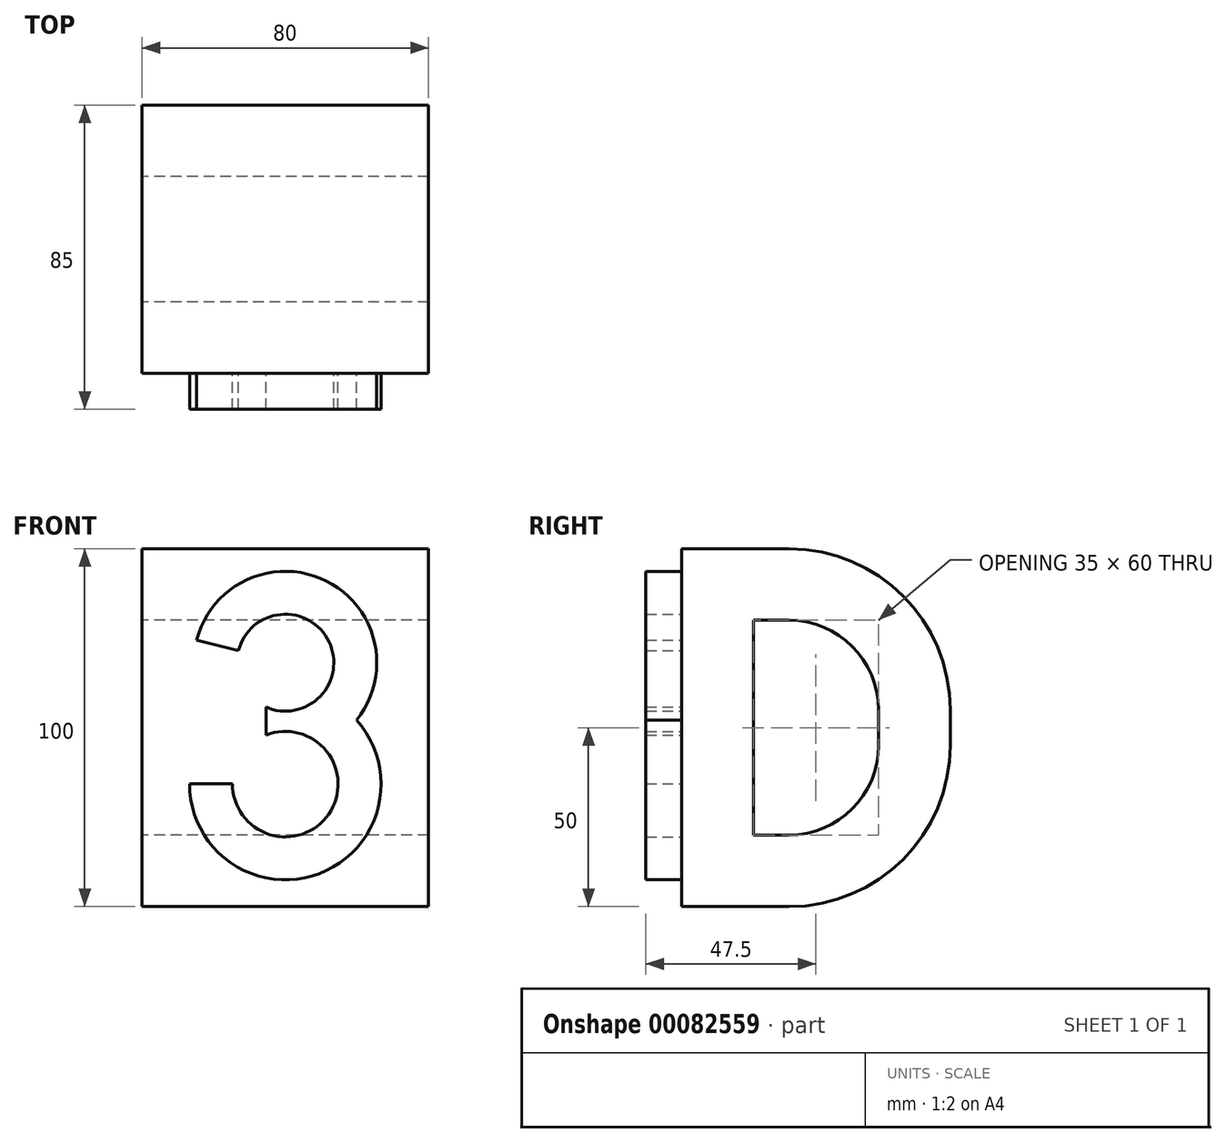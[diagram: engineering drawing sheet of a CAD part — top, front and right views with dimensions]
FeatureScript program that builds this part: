
annotation { "Feature Type Name" : "Feature", "Feature Type Description" : "" }
export const myFeature = defineFeature(function(context is Context, id is Id, definition is map)
    precondition{}
    {
        {
            var Q0;
            Q0=qCreatedBy(makeId("Right.planeOp"),FACE);
            var sketch = newSketch(context, id + "F0", { "sketchPlane" : qUnion([Q0])});
            skLineSegment(sketch, "E0.bottom", {"start": v(0, 0) * mm, "end": v(75, 0) * mm});
            skLineSegment(sketch, "E0.top", {"start": v(0, 100) * mm, "end": v(75, 100) * mm});
            skLineSegment(sketch, "E0.left", {"start": v(0, 0) * mm, "end": v(0, 100) * mm});
            skLineSegment(sketch, "E0.right", {"start": v(75, 0) * mm, "end": v(75, 100) * mm});
            skLineSegment(sketch, "E1.0", {"start": v(20, 80) * mm, "end": v(55, 80) * mm});
            skLineSegment(sketch, "E1.1", {"start": v(20, 20) * mm, "end": v(20, 80) * mm});
            skLineSegment(sketch, "E1.2", {"start": v(20, 20) * mm, "end": v(55, 20) * mm});
            skLineSegment(sketch, "E1.3", {"start": v(55, 20) * mm, "end": v(55, 80) * mm});
            skSolve(sketch);
        }
        {
            var Q0;
            Q0 = qSketchRegion(id + "F0", true);
            extrude(context, id + "F1", {"entities" : qUnion([Q0]), "endBound" : BoundingType.SYMMETRIC, "depth" : 80 * mm});
        }
        {
            var Q0;
            Q0=makeQuery(id+"F1.opExtrude","SWEPT_EDGE",EDGE,{"disambiguationData":[OSD([sQuery(id+"F0.wireOp",EDGE,"E1.0"),sQuery(id+"F0.wireOp",EDGE,"E1.3")])]});
            var Q1;
            Q1=makeQuery(id+"F1.opExtrude","SWEPT_EDGE",EDGE,{"disambiguationData":[OSD([sQuery(id+"F0.wireOp",EDGE,"E1.2"),sQuery(id+"F0.wireOp",EDGE,"E1.3")])]});
            fillet(context, id + "F2", {"entities" : qUnion([Q0, Q1]), "radius" : 25 * mm, "tangentPropagation" : true, "allowEdgeOverflow" : false});
        }
        {
            var Q0;
            Q0=makeQuery(id+"F1.opExtrude","SWEPT_EDGE",EDGE,{"disambiguationData":[OSD([sQuery(id+"F0.wireOp",EDGE,"E0.top"),sQuery(id+"F0.wireOp",EDGE,"E0.right")])]});
            var Q1;
            Q1=makeQuery(id+"F1.opExtrude","SWEPT_EDGE",EDGE,{"disambiguationData":[OSD([sQuery(id+"F0.wireOp",EDGE,"E0.bottom"),sQuery(id+"F0.wireOp",EDGE,"E0.right")])]});
            fillet(context, id + "F3", {"entities" : qUnion([Q0, Q1]), "radius" : 45 * mm, "tangentPropagation" : true, "allowEdgeOverflow" : false});
        }
        {
            var Q0;
            Q0=makeQuery(id+"F1.opExtrude","SWEPT_FACE",FACE,{"disambiguationData":[OSD([sQuery(id+"F0.wireOp",EDGE,"E0.left")])]});
            var sketch = newSketch(context, id + "F4", { "sketchPlane" : qUnion([Q0])});
            skArc(sketch, "E2", {"start": v(19.88, 52.12) * mm, "mid": v(11.45, 90.99) * mm, "end": v(-24.75, 74.48) * mm});
            skArc(sketch, "E3", {"start": v(-26.74, 34.4) * mm, "mid": v(9.5, 9.23) * mm, "end": v(19.88, 52.12) * mm});
            skArc(sketch, "E4.0", {"start": v(-5.43, 55.75) * mm, "mid": v(12.2, 74.05) * mm, "end": v(-13.1, 71.61) * mm});
            skArc(sketch, "E5.0", {"start": v(-14.74, 34.4) * mm, "mid": v(12.15, 25.87) * mm, "end": v(-5.43, 47.94) * mm});
            skLineSegment(sketch, "E6", {"start": v(-13.1, 71.61) * mm, "end": v(-24.75, 74.48) * mm});
            skLineSegment(sketch, "E7", {"start": v(-14.74, 34.4) * mm, "end": v(-26.74, 34.4) * mm});
            skLineSegment(sketch, "E8", {"start": v(-5.43, 55.75) * mm, "end": v(-5.43, 47.94) * mm});
            skSolve(sketch);
        }
        {
            var Q0;
            Q0 = qSketchRegion(id + "F4", true);
            extrude(context, id + "F5", {"entities" : qUnion([Q0]), "operationType" : NewBodyOperationType.ADD, "depth" : 10 * mm});
        }
    });
